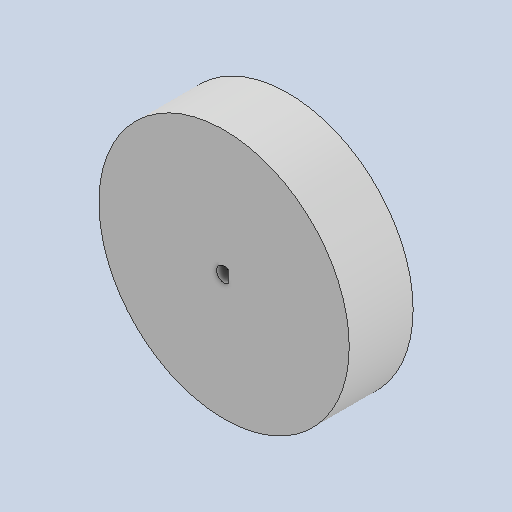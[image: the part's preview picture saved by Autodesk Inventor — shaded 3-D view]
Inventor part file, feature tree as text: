
AUTODESK INVENTOR PART (.ipt)
format: ipt  version: 2023 (Build 270158000, 158)  size: 133,632 bytes
history: native  units: in
note: dims shown in document units (in); Inventor stores cm internally (conversion verified against a paired STEP export)
features: extrude x2, plane x1, other x1, sketch x1
ambient origin geometry x8: Origin, YZ Plane, XZ Plane, XY Plane, X Axis, Y Axis, Z Axis, Center Point
bodies: Solid1 (feature_tree)
feature tree (5):
  plane  "Work Plane2"
  extrude  "Extrusion1"  Depth=0.4724in TaperAngle=0.0deg
  extrude  "Extrusion2"  Depth=0.4724in TaperAngle=0.0deg
  other  "Wheel Sketch"
  sketch  "Sketch2"  dims[d0=1.8504in d3=0.4724in d4=0.0in d7=0.4724in d8=0.0in d9=0.0197in d10=0.0344in d11=0.0197in d12=0.0344in]
